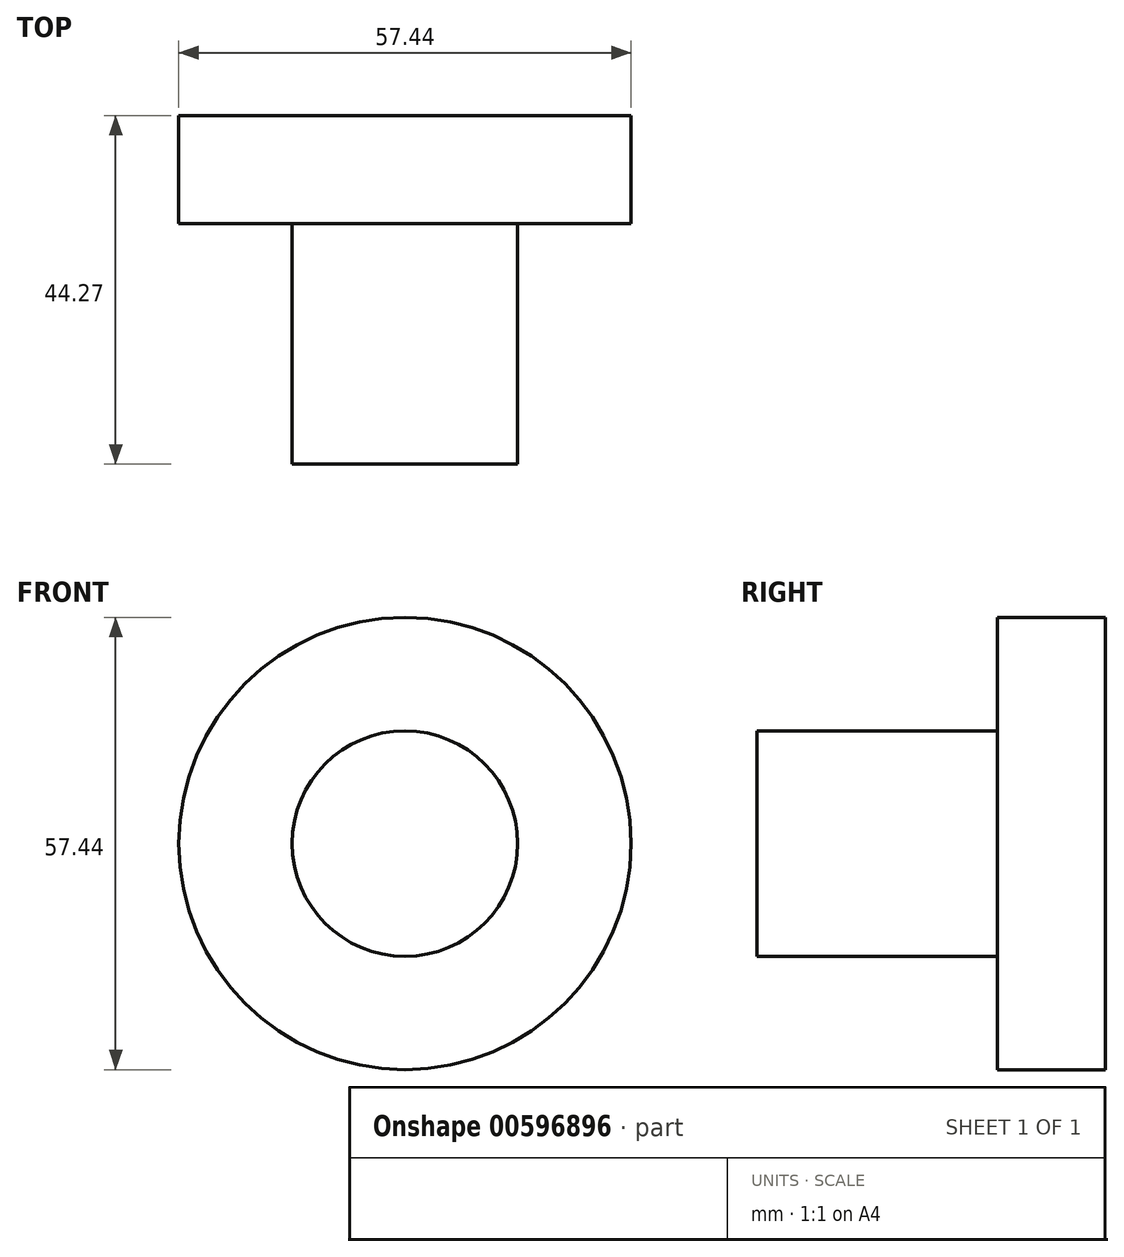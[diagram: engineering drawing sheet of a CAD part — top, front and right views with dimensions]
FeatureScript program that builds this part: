
annotation { "Feature Type Name" : "Feature", "Feature Type Description" : "" }
export const myFeature = defineFeature(function(context is Context, id is Id, definition is map)
    precondition{}
    {
        {
            var Q0;
            Q0=qCreatedBy(makeId("Top.planeOp"),FACE);
            var sketch = newSketch(context, id + "F0", { "sketchPlane" : qUnion([Q0])});
            skLineSegment(sketch, "E0", {"start": v(0, 28.16) * mm, "end": v(0, 0) * mm});
            skLineSegment(sketch, "E1", {"start": v(0, 0) * mm, "end": v(14.31, 0) * mm});
            skLineSegment(sketch, "E2", {"start": v(14.31, 0) * mm, "end": v(14.31, 30.53) * mm});
            skLineSegment(sketch, "E3", {"start": v(14.31, 30.53) * mm, "end": v(28.72, 30.53) * mm});
            skLineSegment(sketch, "E4", {"start": v(28.72, 30.53) * mm, "end": v(28.72, 44.27) * mm});
            skLineSegment(sketch, "E5", {"start": v(28.72, 44.27) * mm, "end": v(0, 44.27) * mm});
            skLineSegment(sketch, "E6", {"start": v(0, 44.27) * mm, "end": v(0, 28.16) * mm});
            skSolve(sketch);
        }
        {
            var Q0;
            Q0=makeQuery(id+"F0.imprint","IMPRINT",FACE,{"disambiguationData":[TD([[makeQuery(id+"F0.imprint","IMPRINT",EDGE,{"derivedFrom":sQuery(id+"F0.wireOp",EDGE,"E0")}),1.0]])]});
            var Q1;
            Q1=sQuery(id+"F0.wireOp",EDGE,"E0");
            revolve(context, id + "F1", {"entities" : qUnion([Q0]), "axis" : qUnion([Q1]), "revolveType" : RevolveType.FULL});
        }
    });
